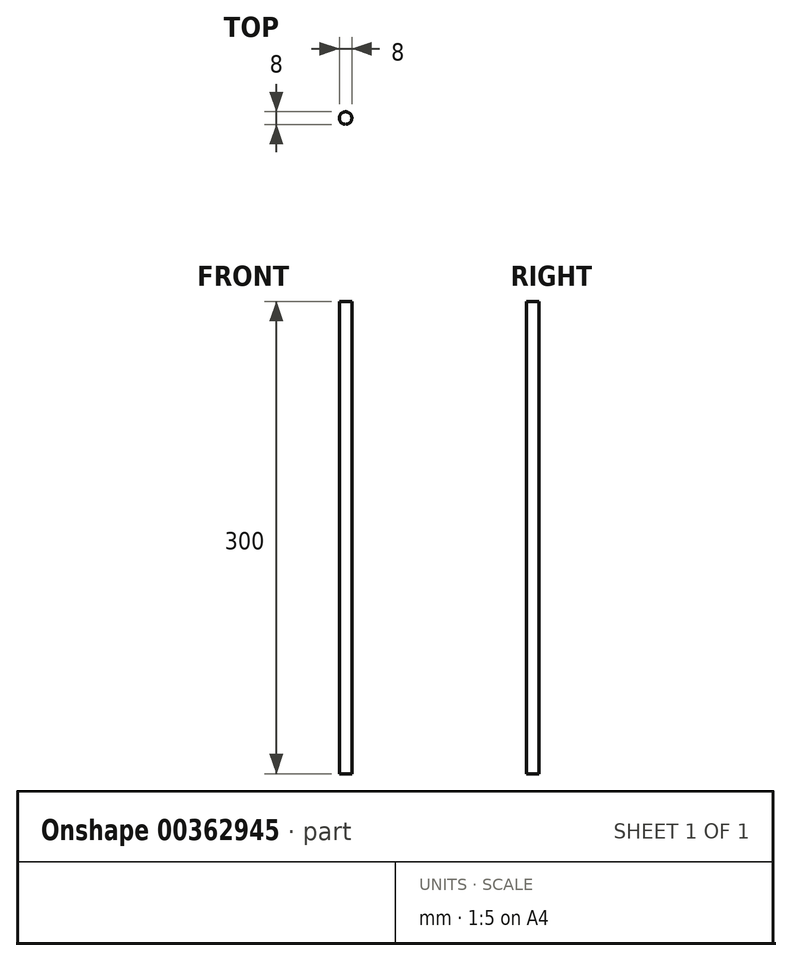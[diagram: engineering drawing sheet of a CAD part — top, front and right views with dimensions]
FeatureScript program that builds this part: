
annotation { "Feature Type Name" : "Feature", "Feature Type Description" : "" }
export const myFeature = defineFeature(function(context is Context, id is Id, definition is map)
    precondition{}
    {
        {
            var Q0;
            Q0=qCreatedBy(makeId("Front.planeOp"),FACE);
            var sketch = newSketch(context, id + "F0", { "sketchPlane" : qUnion([Q0])});
            skLineSegment(sketch, "E0.bottom", {"start": v(-6.16, 256.32) * mm, "end": v(-10.16, 256.32) * mm});
            skLineSegment(sketch, "E0.top", {"start": v(-6.16, -43.68) * mm, "end": v(-10.16, -43.68) * mm});
            skLineSegment(sketch, "E0.left", {"start": v(-6.16, 256.32) * mm, "end": v(-6.16, -43.68) * mm});
            skLineSegment(sketch, "E0.right", {"start": v(-10.16, 256.32) * mm, "end": v(-10.16, -43.68) * mm});
            skSolve(sketch);
        }
        {
            var Q0;
            Q0=makeQuery(id+"F0.imprint","IMPRINT",FACE,{"disambiguationData":[TD([[makeQuery(id+"F0.imprint","IMPRINT",EDGE,{"derivedFrom":sQuery(id+"F0.wireOp",EDGE,"E0.bottom")}),1.0]])]});
            var Q1;
            Q1=sQuery(id+"F0.wireOp",EDGE,"E0.left");
            revolve(context, id + "F1", {"entities" : qUnion([Q0]), "axis" : qUnion([Q1]), "revolveType" : RevolveType.FULL});
        }
    });
